# Revit family: Rail_System-Zoeller-(2pt5_3_Inch)
name_source: partatom
category: Mechanical Equipment
revit_build: Autodesk Revit 2014 (Build: 20130308_1515(x64)
units: mm (PartAtom-declared; Revit-internal decimal feet)

## types (2) — shared parameters
Assembly Code = D2030400
Bracket Height = 60"
CW Connection = Yes
Connection Type = 2-1/2" or 3" Horizontal Flange
Default Elevation = 60"
Description = 3" Guide Rail System SS
HW Connection = No
Manufacturer = Zoeller
Model = 3" Rail System
Price = Prices may vary. Please consult Manufacturer Representative for most up-to-date price list.
Pump Discharge Diameter = 3"
Pump Discharge Radius = 1 1/2"
Rail System Discharge Diameter = 3"
Rail System Discharge Radius = 1 1/2"
URL = http://www.zoellerpumps.com
Vent Connection = No
Waste Connection = Yes

## per-type parameters (varying)
| type | Material | Mounting Plate | Non-Sparking Rail System |
| 39-0094 - 2-1/2" - 3" Rail System | Metal-Zoeller-Epoxy Powder Coated Ductile Iron | Mounting_Plate-Zoeller-Rail_System-C00536 : Mounting Plate | No |
| 39-0095 - 2-1/2" - 3" Non-Sparking Rail Sytem | Brass-Zoeller-Copper Alloy | Mounting_Plate-Zoeller-Rail_System-C00536 : Mounting Plate - C00535 | Yes |

## geometry (parser evidence)
native form markers: Sweep x11
no freeform markers — native parametric forms only
